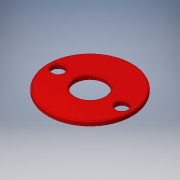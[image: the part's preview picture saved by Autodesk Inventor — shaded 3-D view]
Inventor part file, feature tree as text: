
AUTODESK INVENTOR PART (.ipt)
format: ipt  version: 2016 (Build 200138000, 138)  size: 161,280 bytes
history: native  units: in
note: dims shown in document units (in); Inventor stores cm internally (conversion verified against a paired STEP export)
features: extrude x2, sketch x2, fillet x1
ambient origin geometry x8: Origin, YZ Plane, XZ Plane, XY Plane, X Axis, Y Axis, Z Axis, Center Point
bodies: Solid1 (feature_tree)
feature tree (5):
  extrude  "Extrusion1"  Depth=0.289in
  extrude  "Extrusion3"  Depth=0.3065in
  fillet  "Fillet2"  Radius=0.114in
  sketch  "Sketch1"  dims[d0=0.808in d1=0.289in]
  sketch  "Sketch3"  dims[d2=0.045in d3=0.0in d7=0.3065in d8=0.114in d9=0.7874in d11=360.0deg d13=0.365in d14=0.0in d16=0.01in]
